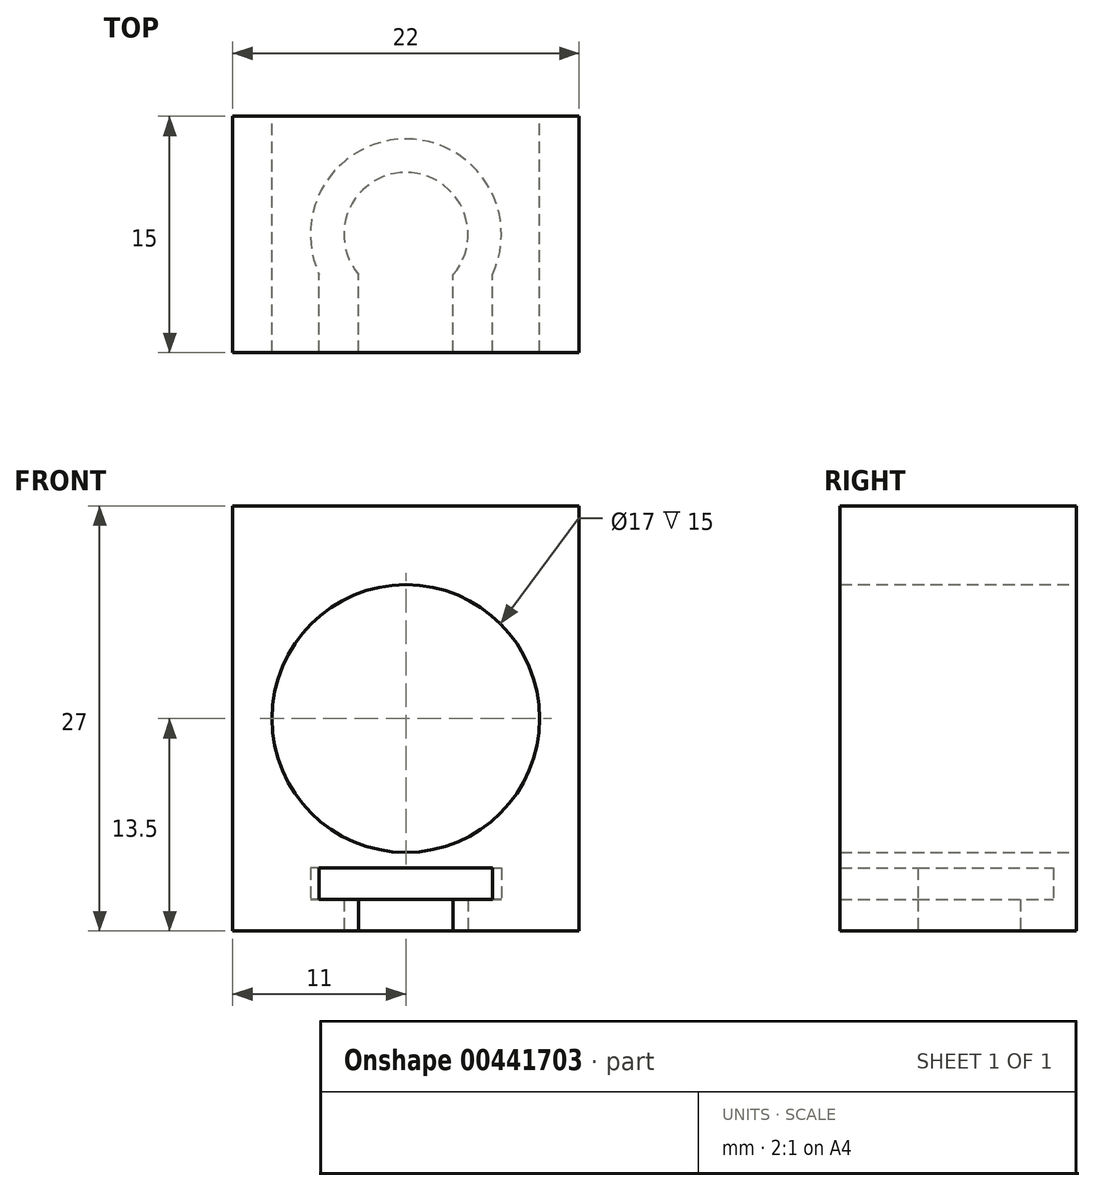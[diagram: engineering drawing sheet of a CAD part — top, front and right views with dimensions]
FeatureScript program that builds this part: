
annotation { "Feature Type Name" : "Feature", "Feature Type Description" : "" }
export const myFeature = defineFeature(function(context is Context, id is Id, definition is map)
    precondition{}
    {
        {
            var Q0;
            Q0=qCreatedBy(makeId("Front.planeOp"),FACE);
            var sketch = newSketch(context, id + "F0", { "sketchPlane" : qUnion([Q0])});
            skLineSegment(sketch, "E0.bottom", {"start": v(-11, -13.5) * mm, "end": v(11, -13.5) * mm});
            skLineSegment(sketch, "E0.top", {"start": v(-11, 13.5) * mm, "end": v(11, 13.5) * mm});
            skLineSegment(sketch, "E0.left", {"start": v(-11, -13.5) * mm, "end": v(-11, 13.5) * mm});
            skLineSegment(sketch, "E0.right", {"start": v(11, -13.5) * mm, "end": v(11, 13.5) * mm});
            skLineSegment(sketch, "E1", {"start": v(0, 18.36) * mm, "end": v(0, -15.6) * mm, "construction": true});
            skLineSegment(sketch, "E2", {"start": v(-16.08, 0) * mm, "end": v(19.05, 0) * mm, "construction": true});
            skCircle(sketch, "E3", {"center": v(0, 0) * mm, "radius": 8.5 * mm});
            skSolve(sketch);
        }
        {
            var Q0;
            Q0 = qSketchRegion(id + "F0", true);
            extrude(context, id + "F1", {"entities" : qUnion([Q0]), "endBound" : BoundingType.SYMMETRIC, "depth" : 15 * mm});
        }
        {
            var Q0;
            Q0=makeQuery(id+"F1.opExtrude","SWEPT_FACE",FACE,{"disambiguationData":[OSD([sQuery(id+"F0.wireOp",EDGE,"E0.bottom")])]});
            var sketch = newSketch(context, id + "F2", { "sketchPlane" : qUnion([Q0])});
            skLineSegment(sketch, "E4", {"start": v(-3, 7.5) * mm, "end": v(-3, 2.56) * mm});
            skLineSegment(sketch, "E5", {"start": v(3, 7.5) * mm, "end": v(3, 2.56) * mm});
            skArc(sketch, "E6", {"start": v(-3, 2.56) * mm, "mid": v(0, -3.94) * mm, "end": v(3, 2.56) * mm});
            skLineSegment(sketch, "E7", {"start": v(0, 10.7) * mm, "end": v(0, -12.84) * mm, "construction": true});
            skSolve(sketch);
        }
        {
            var Q0;
            Q0 = qSketchRegion(id + "F2", true);
            var Q1;
            {var subQ0=sQuery(id+"F2.wireOp",EDGE,"E4");Q1=makeQuery(id+"F2.imprint","IMPRINT",FACE,{"disambiguationData":[TD([[makeQuery(id+"F2.imprint","IMPRINT",EDGE,{"derivedFrom":subQ0}),1.0]])]});}
            extrude(context, id + "F3", {"entities" : qUnion([Q0, Q1]), "operationType" : NewBodyOperationType.REMOVE, "oppositeDirection" : true, "depth" : 2 * mm});
        }
        {
            var Q0;
            Q0=makeQuery(id+"F1.opExtrude","SWEPT_FACE",FACE,{"disambiguationData":[OSD([sQuery(id+"F0.wireOp",EDGE,"E0.bottom")])]});
            cPlane(context, id + "F4", {"entities" : qUnion([Q0]), "cplaneType" : CPlaneType.OFFSET, "offset" : 2 * mm, "oppositeDirection" : true, "width" : 150 * mm, "height" : 150 * mm});
        }
        {
            var Q0;
            Q0=qCreatedBy(id+"F4.planeOp",FACE);
            var sketch = newSketch(context, id + "F5", { "sketchPlane" : qUnion([Q0])});
            skLineSegment(sketch, "E8", {"start": v(-5.5, 7.5) * mm, "end": v(-5.5, 2.56) * mm});
            skLineSegment(sketch, "E9", {"start": v(5.5, 7.5) * mm, "end": v(5.5, 2.56) * mm});
            skLineSegment(sketch, "E10", {"start": v(0, 11.6) * mm, "end": v(0, -12.84) * mm, "construction": true});
            skArc(sketch, "E11", {"start": v(-5.5, 2.56) * mm, "mid": v(0, -6.07) * mm, "end": v(5.5, 2.56) * mm});
            skLineSegment(sketch, "E12", {"start": v(-5.5, 7.5) * mm, "end": v(5.5, 7.5) * mm});
            skSolve(sketch);
        }
        {
            var Q0;
            Q0 = qSketchRegion(id + "F5", true);
            extrude(context, id + "F6", {"entities" : qUnion([Q0]), "operationType" : NewBodyOperationType.REMOVE, "oppositeDirection" : true, "depth" : 2 * mm});
        }
    });
